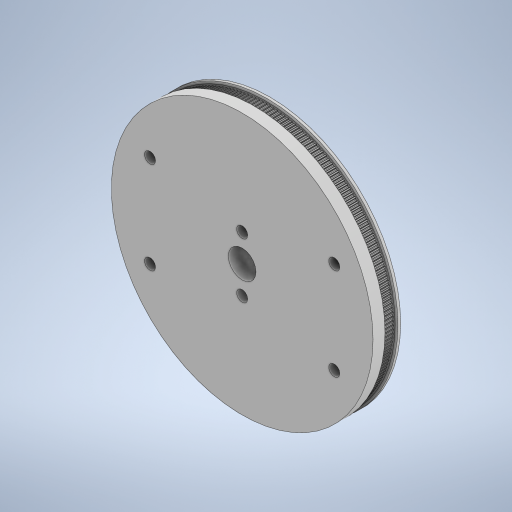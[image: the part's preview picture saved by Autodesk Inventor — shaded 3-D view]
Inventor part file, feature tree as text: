
AUTODESK INVENTOR PART (.ipt)
format: ipt  version: 2024 (Build 280153000, 153)  size: 6,181,888 bytes
history: native  units: mm
features: extrude x4, sketch x3, other x3, reference x2, pattern_circular x1, chamfer x1, mirror x1, projected_geometry x1
ambient origin geometry x8: Origin, YZ Plane, XZ Plane, XY Plane, X Axis, Y Axis, Z Axis, Center Point
bodies: Solid1 (feature_tree)
feature tree (16):
  extrude  "Extrusion1"  Depth=0.143885mm
  pattern_circular  "Circular Pattern1"  [2 undecoded]
  extrude  "Extrusion2"  Depth=0.555mm
  chamfer  "Chamfer1"  Distance=1.0mm
  mirror  "Mirror1"
  extrude  "Extrusion3"  Depth=0.15mm
  extrude  "Extrusion4"  Depth=0.6mm
  sketch  "Sketch1"  dims[d0=139.0mm d1=0.143885mm]
  sketch  "Sketch4"  dims[d2=0.057554mm]
  reference  "Reference1"
  reference  "Reference2"
  sketch  "Sketch5"  dims[d3=1.004mm d4=0.75mm d5=0.555mm d6=1.0mm d7=0.15mm d9=0.6mm d10=6.0mm d11=0.0mm d12=2183.406894mm d13=360.0deg d15=142.0mm d16=2.0mm d17=0.0mm d18=1.0mm d19=0.5mm d20=45.0deg d21=5.0mm d26=0.0mm d27=0.0mm d28=5.0mm d29=0.0mm]
  projected_geometry  "Projected Loop1"
  other  "<userpath>\Documents\Inventor\robot arm\base_assembly.iam"
  other  "base_assembly.iam"
  other  "base-top-plate:1"
note: 2 required parameter values undecoded (feature->parameter linkage not recoverable at this tier; creation-order binding heuristic only, values carry confidence <= 0.55)
